# Revit family: 540_Sliding_Window_XO_Standard
name_source: partatom
category: Windows
revit_build: Autodesk Revit 2014 (Build: 20130308_1515(x64)
units: mm (PartAtom-declared; Revit-internal decimal feet)

## types (72) — shared parameters
Centered In Wall = Yes
Custom Sash Width Left = 600 mm  [stored 1.9685 ft]
Default Sill Height = 800 mm
Description = Sliding window, XO
Equal Sash Width = Yes
Frame Thickness = 54 mm  [stored 0.177165 ft]
Limit Sash Height Max = 1500 mm  [stored 4.92126 ft]
Limit Sash Height Min = 300 mm  [stored 0.984252 ft]
Limit Sash Width Max = 1200 mm
Limit Sash Width Min = 300 mm  [stored 0.984252 ft]
Limit Window Height Max = 1580 mm
Limit Window Height Min = 380 mm
Limit Window Width Max = 2418 mm
Limit Window Width Min = 618 mm
Manufacturer = Crealco
Model = 540
Rough Width = 3 mm  [stored 0.00984252 ft]
Sash Frame Seal = 3 mm  [stored 0.00984252 ft]
URL = http://www.crealco.co.za
Wall Closure = By host
zero-valued in all types: Custom Frame Offset From Exterior

## per-type parameters (varying)
- 540SW-0906XO-1000Pa: Area Left Sash Glazing=0.13 m²; Area Right Sash Glazing=0.13 m²; Clearvue SHGC Value=0.399; Clearvue U Value=7.41; Custom Windload=1000 mm  [stored 3.28084 ft]; Custom Window Height=590 mm  [stored 1.9357 ft]; Custom Window Width=890 mm  [stored 2.91995 ft]; Energy Advantage SHGC Value=0.361; Energy Advantage U Value=6.43; Heavy Duty Interlocker=No; Height=590 mm  [stored 1.9357 ft]; Intruderprufe LowE SHGC Value=0.339; Intruderprufe LowE U Value=6.32; Intruderprufe SHGC Value=0.378; Intruderprufe U Value=7.24; Is Heavy Duty Interlocker=0 mm  [stored 0 ft]; Limit Sash Width Left Max=572 mm; Limit Sash Width Left Min=300 mm  [stored 0.984252 ft]; Max Pane Area=0.13 m²; Sash Height=510 mm; Sash Width Left=436 mm; Sash Width Right=436 mm; Standard Interlocker=Yes; Width=890 mm  [stored 2.91995 ft]; Windload Design=1000 mm  [stored 3.28084 ft]
- 540SW-1206XO-1000Pa: Area Left Sash Glazing=0.19 m²; Area Right Sash Glazing=0.19 m²; Clearvue SHGC Value=0.44; Clearvue U Value=7.19; Custom Windload=1000 mm  [stored 3.28084 ft]; Custom Window Height=590 mm  [stored 1.9357 ft]; Custom Window Width=1190 mm  [stored 3.9042 ft]; Energy Advantage SHGC Value=0.397; Energy Advantage U Value=6.12; Heavy Duty Interlocker=No; Height=590 mm  [stored 1.9357 ft]; Intruderprufe LowE SHGC Value=0.372; Intruderprufe LowE U Value=6.02; Intruderprufe SHGC Value=0.416; Intruderprufe U Value=7.04; Is Heavy Duty Interlocker=0 mm  [stored 0 ft]; Limit Sash Width Left Max=872 mm; Limit Sash Width Left Min=300 mm  [stored 0.984252 ft]; Max Pane Area=0.19 m²; Sash Height=510 mm; Sash Width Left=586 mm; Sash Width Right=586 mm; Standard Interlocker=Yes; Width=1190 mm  [stored 3.9042 ft]; Windload Design=1000 mm  [stored 3.28084 ft]
- 540SW-1506XO-1000Pa: Area Left Sash Glazing=0.25 m²; Area Right Sash Glazing=0.25 m²; Clearvue SHGC Value=0.464; Clearvue U Value=7.07; Custom Windload=1000 mm  [stored 3.28084 ft]; Custom Window Height=590 mm  [stored 1.9357 ft]; Custom Window Width=1490 mm  [stored 4.88845 ft]; Energy Advantage SHGC Value=0.418; Energy Advantage U Value=5.93; Heavy Duty Interlocker=No; Height=590 mm  [stored 1.9357 ft]; Intruderprufe LowE SHGC Value=0.392; Intruderprufe LowE U Value=5.83; Intruderprufe SHGC Value=0.439; Intruderprufe U Value=6.93; Is Heavy Duty Interlocker=0 mm  [stored 0 ft]; Limit Sash Width Left Max=1172 mm; Limit Sash Width Left Min=300 mm  [stored 0.984252 ft]; Max Pane Area=0.25 m²; Sash Height=510 mm; Sash Width Left=736 mm; Sash Width Right=736 mm; Standard Interlocker=Yes; Width=1490 mm  [stored 4.88845 ft]; Windload Design=1000 mm  [stored 3.28084 ft]
- 540SW-1806XO-1000Pa: Area Left Sash Glazing=0.31 m²; Area Right Sash Glazing=0.31 m²; Clearvue SHGC Value=0.481; Clearvue U Value=6.98; Custom Windload=1000 mm  [stored 3.28084 ft]; Custom Window Height=590 mm  [stored 1.9357 ft]; Custom Window Width=1790 mm  [stored 5.8727 ft]; Energy Advantage SHGC Value=0.433; Energy Advantage U Value=5.81; Heavy Duty Interlocker=No; Height=590 mm  [stored 1.9357 ft]; Intruderprufe LowE SHGC Value=0.405; Intruderprufe LowE U Value=5.71; Intruderprufe SHGC Value=0.454; Intruderprufe U Value=6.85; Is Heavy Duty Interlocker=0 mm  [stored 0 ft]; Limit Sash Width Left Max=1200 mm; Limit Sash Width Left Min=572 mm; Max Pane Area=0.31 m²; Sash Height=510 mm; Sash Width Left=886 mm; Sash Width Right=886 mm; Standard Interlocker=Yes; Width=1790 mm  [stored 5.8727 ft]; Windload Design=1000 mm  [stored 3.28084 ft]
- 540SW-2106XO-1000Pa: Area Left Sash Glazing=0.37 m²; Area Right Sash Glazing=0.37 m²; Clearvue SHGC Value=0.492; Clearvue U Value=6.92; Custom Windload=1000 mm  [stored 3.28084 ft]; Custom Window Height=590 mm  [stored 1.9357 ft]; Custom Window Width=2090 mm  [stored 6.85696 ft]; Energy Advantage SHGC Value=0.443; Energy Advantage U Value=5.72; Heavy Duty Interlocker=No; Height=590 mm  [stored 1.9357 ft]; Intruderprufe LowE SHGC Value=0.414; Intruderprufe LowE U Value=5.62; Intruderprufe SHGC Value=0.465; Intruderprufe U Value=6.79; Is Heavy Duty Interlocker=0 mm  [stored 0 ft]; Limit Sash Width Left Max=1200 mm; Limit Sash Width Left Min=872 mm; Max Pane Area=0.37 m²; Sash Height=510 mm; Sash Width Left=1036 mm; Sash Width Right=1036 mm; Standard Interlocker=Yes; Width=2090 mm  [stored 6.85696 ft]; Windload Design=1000 mm  [stored 3.28084 ft]
- 540SW-2406XO-1000Pa: Area Left Sash Glazing=0.43 m²; Area Right Sash Glazing=0.43 m²; Clearvue SHGC Value=0.501; Clearvue U Value=6.88; Custom Windload=1000 mm  [stored 3.28084 ft]; Custom Window Height=590 mm  [stored 1.9357 ft]; Custom Window Width=2390 mm  [stored 7.84121 ft]; Energy Advantage SHGC Value=0.45; Energy Advantage U Value=5.65; Heavy Duty Interlocker=No; Height=590 mm  [stored 1.9357 ft]; Intruderprufe LowE SHGC Value=0.421; Intruderprufe LowE U Value=5.56; Intruderprufe SHGC Value=0.473; Intruderprufe U Value=6.75; Is Heavy Duty Interlocker=0 mm  [stored 0 ft]; Limit Sash Width Left Max=1200 mm; Limit Sash Width Left Min=1172 mm; Max Pane Area=0.43 m²; Sash Height=510 mm; Sash Width Left=1186 mm; Sash Width Right=1186 mm; Standard Interlocker=Yes; Width=2390 mm  [stored 7.84121 ft]; Windload Design=1000 mm  [stored 3.28084 ft]
- 540SW-0909XO-1000Pa: Area Left Sash Glazing=0.23 m²; Area Right Sash Glazing=0.23 m²; Clearvue SHGC Value=0.465; Clearvue U Value=7.33; Custom Windload=1000 mm  [stored 3.28084 ft]; Custom Window Height=890 mm  [stored 2.91995 ft]; Custom Window Width=890 mm  [stored 2.91995 ft]; Energy Advantage SHGC Value=0.419; Energy Advantage U Value=6.16; Heavy Duty Interlocker=No; Height=890 mm  [stored 2.91995 ft]; Intruderprufe LowE SHGC Value=0.392; Intruderprufe LowE U Value=6.06; Intruderprufe SHGC Value=0.44; Intruderprufe U Value=7.16; Is Heavy Duty Interlocker=0 mm  [stored 0 ft]; Limit Sash Width Left Max=572 mm; Limit Sash Width Left Min=300 mm  [stored 0.984252 ft]; Max Pane Area=0.23 m²; Sash Height=810 mm  [stored 2.65748 ft]; Sash Width Left=436 mm; Sash Width Right=436 mm; Standard Interlocker=Yes; Width=890 mm  [stored 2.91995 ft]; Windload Design=1000 mm  [stored 3.28084 ft]
- 540SW-1209XO-1000Pa: Area Left Sash Glazing=0.34 m²; Area Right Sash Glazing=0.34 m²; Clearvue SHGC Value=0.514; Clearvue U Value=7.08; Custom Windload=1000 mm  [stored 3.28084 ft]; Custom Window Height=890 mm  [stored 2.91995 ft]; Custom Window Width=1190 mm  [stored 3.9042 ft]; Energy Advantage SHGC Value=0.462; Energy Advantage U Value=5.79; Heavy Duty Interlocker=No; Height=890 mm  [stored 2.91995 ft]; Intruderprufe LowE SHGC Value=0.432; Intruderprufe LowE U Value=5.69; Intruderprufe SHGC Value=0.485; Intruderprufe U Value=6.92; Is Heavy Duty Interlocker=0 mm  [stored 0 ft]; Limit Sash Width Left Max=872 mm; Limit Sash Width Left Min=300 mm  [stored 0.984252 ft]; Max Pane Area=0.34 m²; Sash Height=810 mm  [stored 2.65748 ft]; Sash Width Left=586 mm; Sash Width Right=586 mm; Standard Interlocker=Yes; Width=1190 mm  [stored 3.9042 ft]; Windload Design=1000 mm  [stored 3.28084 ft]
- 540SW-1509XO-1000Pa: Area Left Sash Glazing=0.44 m²; Area Right Sash Glazing=0.44 m²; Clearvue SHGC Value=0.543; Clearvue U Value=6.93; Custom Windload=1000 mm  [stored 3.28084 ft]; Custom Window Height=890 mm  [stored 2.91995 ft]; Custom Window Width=1490 mm  [stored 4.88845 ft]; Energy Advantage SHGC Value=0.488; Energy Advantage U Value=5.57; Heavy Duty Interlocker=No; Height=890 mm  [stored 2.91995 ft]; Intruderprufe LowE SHGC Value=0.456; Intruderprufe LowE U Value=5.47; Intruderprufe SHGC Value=0.512; Intruderprufe U Value=6.78; Is Heavy Duty Interlocker=0 mm  [stored 0 ft]; Limit Sash Width Left Max=1172 mm; Limit Sash Width Left Min=300 mm  [stored 0.984252 ft]; Max Pane Area=0.44 m²; Sash Height=810 mm  [stored 2.65748 ft]; Sash Width Left=736 mm; Sash Width Right=736 mm; Standard Interlocker=Yes; Width=1490 mm  [stored 4.88845 ft]; Windload Design=1000 mm  [stored 3.28084 ft]
- 540SW-1809XO-1000Pa: Area Left Sash Glazing=0.55 m²; Area Right Sash Glazing=0.55 m²; Clearvue SHGC Value=0.562; Clearvue U Value=6.83; Custom Windload=1000 mm  [stored 3.28084 ft]; Custom Window Height=890 mm  [stored 2.91995 ft]; Custom Window Width=1790 mm  [stored 5.8727 ft]; Energy Advantage SHGC Value=0.505; Energy Advantage U Value=5.42; Heavy Duty Interlocker=No; Height=890 mm  [stored 2.91995 ft]; Intruderprufe LowE SHGC Value=0.471; Intruderprufe LowE U Value=5.33; Intruderprufe SHGC Value=0.531; Intruderprufe U Value=6.68; Is Heavy Duty Interlocker=0 mm  [stored 0 ft]; Limit Sash Width Left Max=1200 mm; Limit Sash Width Left Min=572 mm; Max Pane Area=0.55 m²; Sash Height=810 mm  [stored 2.65748 ft]; Sash Width Left=886 mm; Sash Width Right=886 mm; Standard Interlocker=Yes; Width=1790 mm  [stored 5.8727 ft]; Windload Design=1000 mm  [stored 3.28084 ft]
- 540SW-2109XO-1000Pa: Area Left Sash Glazing=0.65 m²; Area Right Sash Glazing=0.65 m²; Clearvue SHGC Value=0.576; Clearvue U Value=6.76; Custom Windload=1000 mm  [stored 3.28084 ft]; Custom Window Height=890 mm  [stored 2.91995 ft]; Custom Window Width=2090 mm  [stored 6.85696 ft]; Energy Advantage SHGC Value=0.517; Energy Advantage U Value=5.32; Heavy Duty Interlocker=No; Height=890 mm  [stored 2.91995 ft]; Intruderprufe LowE SHGC Value=0.483; Intruderprufe LowE U Value=5.22; Intruderprufe SHGC Value=0.543; Intruderprufe U Value=6.62; Is Heavy Duty Interlocker=0 mm  [stored 0 ft]; Limit Sash Width Left Max=1200 mm; Limit Sash Width Left Min=872 mm; Max Pane Area=0.65 m²; Sash Height=810 mm  [stored 2.65748 ft]; Sash Width Left=1036 mm; Sash Width Right=1036 mm; Standard Interlocker=Yes; Width=2090 mm  [stored 6.85696 ft]; Windload Design=1000 mm  [stored 3.28084 ft]
- 540SW-2409XO-1000Pa: Area Left Sash Glazing=0.76 m²; Area Right Sash Glazing=0.76 m²; Clearvue SHGC Value=0.586; Clearvue U Value=6.7; Custom Windload=1000 mm  [stored 3.28084 ft]; Custom Window Height=890 mm  [stored 2.91995 ft]; Custom Window Width=2390 mm  [stored 7.84121 ft]; Energy Advantage SHGC Value=0.526; Energy Advantage U Value=5.24; Heavy Duty Interlocker=No; Height=890 mm  [stored 2.91995 ft]; Intruderprufe LowE SHGC Value=0.491; Intruderprufe LowE U Value=5.15; Intruderprufe SHGC Value=0.553; Intruderprufe U Value=6.57; Is Heavy Duty Interlocker=0 mm  [stored 0 ft]; Limit Sash Width Left Max=1200 mm; Limit Sash Width Left Min=1172 mm; Max Pane Area=0.76 m²; Sash Height=810 mm  [stored 2.65748 ft]; Sash Width Left=1186 mm; Sash Width Right=1186 mm; Standard Interlocker=Yes; Width=2390 mm  [stored 7.84121 ft]; Windload Design=1000 mm  [stored 3.28084 ft]
- 540SW-0912XO-1000Pa: Area Left Sash Glazing=0.33 m²; Area Right Sash Glazing=0.33 m²; Clearvue SHGC Value=0.497; Clearvue U Value=7.29; Custom Windload=1000 mm  [stored 3.28084 ft]; Custom Window Height=1190 mm  [stored 3.9042 ft]; Custom Window Width=890 mm  [stored 2.91995 ft]; Energy Advantage SHGC Value=0.447; Energy Advantage U Value=6.02; Heavy Duty Interlocker=No; Height=1190 mm  [stored 3.9042 ft]; Intruderprufe LowE SHGC Value=0.419; Intruderprufe LowE U Value=5.92; Intruderprufe SHGC Value=0.47; Intruderprufe U Value=7.12; Is Heavy Duty Interlocker=0 mm  [stored 0 ft]; Limit Sash Width Left Max=572 mm; Limit Sash Width Left Min=300 mm  [stored 0.984252 ft]; Max Pane Area=0.33 m²; Sash Height=1110 mm  [stored 3.64173 ft]; Sash Width Left=436 mm; Sash Width Right=436 mm; Standard Interlocker=Yes; Width=890 mm  [stored 2.91995 ft]; Windload Design=1000 mm  [stored 3.28084 ft]
- 540SW-1212XO-1000Pa: Area Left Sash Glazing=0.48 m²; Area Right Sash Glazing=0.48 m²; Clearvue SHGC Value=0.55; Clearvue U Value=7.02; Custom Windload=1000 mm  [stored 3.28084 ft]; Custom Window Height=1190 mm  [stored 3.9042 ft]; Custom Window Width=1190 mm  [stored 3.9042 ft]; Energy Advantage SHGC Value=0.494; Energy Advantage U Value=5.62; Heavy Duty Interlocker=No; Height=1190 mm  [stored 3.9042 ft]; Intruderprufe LowE SHGC Value=0.462; Intruderprufe LowE U Value=5.53; Intruderprufe SHGC Value=0.519; Intruderprufe U Value=6.86; Is Heavy Duty Interlocker=0 mm  [stored 0 ft]; Limit Sash Width Left Max=872 mm; Limit Sash Width Left Min=300 mm  [stored 0.984252 ft]; Max Pane Area=0.48 m²; Sash Height=1110 mm  [stored 3.64173 ft]; Sash Width Left=586 mm; Sash Width Right=586 mm; Standard Interlocker=Yes; Width=1190 mm  [stored 3.9042 ft]; Windload Design=1000 mm  [stored 3.28084 ft]
- 540SW-1512XO-1000Pa: Area Left Sash Glazing=0.63 m²; Area Right Sash Glazing=0.63 m²; Clearvue SHGC Value=0.582; Clearvue U Value=6.86; Custom Windload=1000 mm  [stored 3.28084 ft]; Custom Window Height=1190 mm  [stored 3.9042 ft]; Custom Window Width=1490 mm  [stored 4.88845 ft]; Energy Advantage SHGC Value=0.522; Energy Advantage U Value=5.39; Heavy Duty Interlocker=No; Height=1190 mm  [stored 3.9042 ft]; Intruderprufe LowE SHGC Value=0.487; Intruderprufe LowE U Value=5.29; Intruderprufe SHGC Value=0.549; Intruderprufe U Value=6.71; Is Heavy Duty Interlocker=0 mm  [stored 0 ft]; Limit Sash Width Left Max=1172 mm; Limit Sash Width Left Min=300 mm  [stored 0.984252 ft]; Max Pane Area=0.63 m²; Sash Height=1110 mm  [stored 3.64173 ft]; Sash Width Left=736 mm; Sash Width Right=736 mm; Standard Interlocker=Yes; Width=1490 mm  [stored 4.88845 ft]; Windload Design=1000 mm  [stored 3.28084 ft]
- 540SW-1812XO-1000Pa: Area Left Sash Glazing=0.78 m²; Area Right Sash Glazing=0.78 m²; Clearvue SHGC Value=0.603; Clearvue U Value=6.75; Custom Windload=1000 mm  [stored 3.28084 ft]; Custom Window Height=1190 mm  [stored 3.9042 ft]; Custom Window Width=1790 mm  [stored 5.8727 ft]; Energy Advantage SHGC Value=0.54; Energy Advantage U Value=5.23; Heavy Duty Interlocker=No; Height=1190 mm  [stored 3.9042 ft]; Intruderprufe LowE SHGC Value=0.504; Intruderprufe LowE U Value=5.14; Intruderprufe SHGC Value=0.568; Intruderprufe U Value=6.61; Is Heavy Duty Interlocker=0 mm  [stored 0 ft]; Limit Sash Width Left Max=1200 mm; Limit Sash Width Left Min=572 mm; Max Pane Area=0.78 m²; Sash Height=1110 mm  [stored 3.64173 ft]; Sash Width Left=886 mm; Sash Width Right=886 mm; Standard Interlocker=Yes; Width=1790 mm  [stored 5.8727 ft]; Windload Design=1000 mm  [stored 3.28084 ft]
- 540SW-2112XO-1000Pa: Area Left Sash Glazing=0.93 m²; Area Right Sash Glazing=0.93 m²; Clearvue SHGC Value=0.617; Clearvue U Value=6.68; Custom Windload=1000 mm  [stored 3.28084 ft]; Custom Window Height=1190 mm  [stored 3.9042 ft]; Custom Window Width=2090 mm  [stored 6.85696 ft]; Energy Advantage SHGC Value=0.554; Energy Advantage U Value=5.12; Heavy Duty Interlocker=No; Height=1190 mm  [stored 3.9042 ft]; Intruderprufe LowE SHGC Value=0.516; Intruderprufe LowE U Value=5.03; Intruderprufe SHGC Value=0.582; Intruderprufe U Value=6.53; Is Heavy Duty Interlocker=0 mm  [stored 0 ft]; Limit Sash Width Left Max=1200 mm; Limit Sash Width Left Min=872 mm; Max Pane Area=0.93 m²; Sash Height=1110 mm  [stored 3.64173 ft]; Sash Width Left=1036 mm; Sash Width Right=1036 mm; Standard Interlocker=Yes; Width=2090 mm  [stored 6.85696 ft]; Windload Design=1000 mm  [stored 3.28084 ft]
- 540SW-2412XO-1000Pa: Area Left Sash Glazing=1.08 m²; Area Right Sash Glazing=1.08 m²; Clearvue SHGC Value=0.629; Clearvue U Value=6.62; Custom Windload=1000 mm  [stored 3.28084 ft]; Custom Window Height=1190 mm  [stored 3.9042 ft]; Custom Window Width=2390 mm  [stored 7.84121 ft]; Energy Advantage SHGC Value=0.564; Energy Advantage U Value=5.03; Heavy Duty Interlocker=No; Height=1190 mm  [stored 3.9042 ft]; Intruderprufe LowE SHGC Value=0.525; Intruderprufe LowE U Value=4.94; Intruderprufe SHGC Value=0.593; Intruderprufe U Value=6.48; Is Heavy Duty Interlocker=0 mm  [stored 0 ft]; Limit Sash Width Left Max=1200 mm; Limit Sash Width Left Min=1172 mm; Max Pane Area=1.08 m²; Sash Height=1110 mm  [stored 3.64173 ft]; Sash Width Left=1186 mm; Sash Width Right=1186 mm; Standard Interlocker=Yes; Width=2390 mm  [stored 7.84121 ft]; Windload Design=1000 mm  [stored 3.28084 ft]
- 540SW-0915XO-1000Pa: Area Left Sash Glazing=0.43 m²; Area Right Sash Glazing=0.43 m²; Clearvue SHGC Value=0.517; Clearvue U Value=7.27; Custom Windload=1000 mm  [stored 3.28084 ft]; Custom Window Height=1490 mm  [stored 4.88845 ft]; Custom Window Width=890 mm  [stored 2.91995 ft]; Energy Advantage SHGC Value=0.465; Energy Advantage U Value=5.94; Heavy Duty Interlocker=No; Height=1490 mm  [stored 4.88845 ft]; Intruderprufe LowE SHGC Value=0.435; Intruderprufe LowE U Value=5.84; Intruderprufe SHGC Value=0.488; Intruderprufe U Value=7.09; Is Heavy Duty Interlocker=0 mm  [stored 0 ft]; Limit Sash Width Left Max=572 mm; Limit Sash Width Left Min=300 mm  [stored 0.984252 ft]; Max Pane Area=0.43 m²; Sash Height=1410 mm; Sash Width Left=436 mm; Sash Width Right=436 mm; Standard Interlocker=Yes; Width=890 mm  [stored 2.91995 ft]; Windload Design=1000 mm  [stored 3.28084 ft]
- 540SW-1215XO-1000Pa: Area Left Sash Glazing=0.62 m²; Area Right Sash Glazing=0.62 m²; Clearvue SHGC Value=0.572; Clearvue U Value=6.99; Custom Windload=1000 mm  [stored 3.28084 ft]; Custom Window Height=1490 mm  [stored 4.88845 ft]; Custom Window Width=1190 mm  [stored 3.9042 ft]; Energy Advantage SHGC Value=0.513; Energy Advantage U Value=5.53; Heavy Duty Interlocker=No; Height=1490 mm  [stored 4.88845 ft]; Intruderprufe LowE SHGC Value=0.479; Intruderprufe LowE U Value=5.43; Intruderprufe SHGC Value=0.54; Intruderprufe U Value=6.82; Is Heavy Duty Interlocker=0 mm  [stored 0 ft]; Limit Sash Width Left Max=872 mm; Limit Sash Width Left Min=300 mm  [stored 0.984252 ft]; Max Pane Area=0.62 m²; Sash Height=1410 mm; Sash Width Left=586 mm; Sash Width Right=586 mm; Standard Interlocker=Yes; Width=1190 mm  [stored 3.9042 ft]; Windload Design=1000 mm  [stored 3.28084 ft]
- 540SW-1515XO-1000Pa: Area Left Sash Glazing=0.82 m²; Area Right Sash Glazing=0.82 m²; Clearvue SHGC Value=0.605; Clearvue U Value=6.82; Custom Windload=1000 mm  [stored 3.28084 ft]; Custom Window Height=1490 mm  [stored 4.88845 ft]; Custom Window Width=1490 mm  [stored 4.88845 ft]; Energy Advantage SHGC Value=0.542; Energy Advantage U Value=5.28; Heavy Duty Interlocker=Yes; Height=1490 mm  [stored 4.88845 ft]; Intruderprufe LowE SHGC Value=0.506; Intruderprufe LowE U Value=5.19; Intruderprufe SHGC Value=0.571; Intruderprufe U Value=6.66; Is Heavy Duty Interlocker=1 mm  [stored 0.00328084 ft]; Limit Sash Width Left Max=1172 mm; Limit Sash Width Left Min=300 mm  [stored 0.984252 ft]; Max Pane Area=0.82 m²; Sash Height=1410 mm; Sash Width Left=736 mm; Sash Width Right=736 mm; Standard Interlocker=No; Width=1490 mm  [stored 4.88845 ft]; Windload Design=1000 mm  [stored 3.28084 ft]
- 540SW-1815XO-1000Pa: Area Left Sash Glazing=1.01 m²; Area Right Sash Glazing=1.01 m²; Clearvue SHGC Value=0.627; Clearvue U Value=6.71; Custom Windload=1000 mm  [stored 3.28084 ft]; Custom Window Height=1490 mm  [stored 4.88845 ft]; Custom Window Width=1790 mm  [stored 5.8727 ft]; Energy Advantage SHGC Value=0.562; Energy Advantage U Value=5.11; Heavy Duty Interlocker=Yes; Height=1490 mm  [stored 4.88845 ft]; Intruderprufe LowE SHGC Value=0.524; Intruderprufe LowE U Value=5.02; Intruderprufe SHGC Value=0.591; Intruderprufe U Value=6.56; Is Heavy Duty Interlocker=1 mm  [stored 0.00328084 ft]; Limit Sash Width Left Max=1200 mm; Limit Sash Width Left Min=572 mm; Max Pane Area=1.01 m²; Sash Height=1410 mm; Sash Width Left=886 mm; Sash Width Right=886 mm; Standard Interlocker=No; Width=1790 mm  [stored 5.8727 ft]; Windload Design=1000 mm  [stored 3.28084 ft]
- 540SW-2115XO-1000Pa: Area Left Sash Glazing=1.21 m²; Area Right Sash Glazing=1.21 m²; Clearvue SHGC Value=0.642; Clearvue U Value=6.63; Custom Windload=1000 mm  [stored 3.28084 ft]; Custom Window Height=1490 mm  [stored 4.88845 ft]; Custom Window Width=2090 mm  [stored 6.85696 ft]; Energy Advantage SHGC Value=0.576; Energy Advantage U Value=5; Heavy Duty Interlocker=Yes; Height=1490 mm  [stored 4.88845 ft]; Intruderprufe LowE SHGC Value=0.536; Intruderprufe LowE U Value=4.91; Intruderprufe SHGC Value=0.606; Intruderprufe U Value=6.48; Is Heavy Duty Interlocker=1 mm  [stored 0.00328084 ft]; Limit Sash Width Left Max=1200 mm; Limit Sash Width Left Min=872 mm; Max Pane Area=1.21 m²; Sash Height=1410 mm; Sash Width Left=1036 mm; Sash Width Right=1036 mm; Standard Interlocker=No; Width=2090 mm  [stored 6.85696 ft]; Windload Design=1000 mm  [stored 3.28084 ft]
- 540SW-2415XO-1000Pa: Area Left Sash Glazing=1.4 m²; Area Right Sash Glazing=1.4 m²; Clearvue SHGC Value=0.654; Clearvue U Value=6.57; Custom Windload=1000 mm  [stored 3.28084 ft]; Custom Window Height=1490 mm  [stored 4.88845 ft]; Custom Window Width=2390 mm  [stored 7.84121 ft]; Energy Advantage SHGC Value=0.586; Energy Advantage U Value=4.91; Heavy Duty Interlocker=Yes; Height=1490 mm  [stored 4.88845 ft]; Intruderprufe LowE SHGC Value=0.546; Intruderprufe LowE U Value=4.82; Intruderprufe SHGC Value=0.617; Intruderprufe U Value=6.43; Is Heavy Duty Interlocker=1 mm  [stored 0.00328084 ft]; Limit Sash Width Left Max=1200 mm; Limit Sash Width Left Min=1172 mm; Max Pane Area=1.4 m²; Sash Height=1410 mm; Sash Width Left=1186 mm; Sash Width Right=1186 mm; Standard Interlocker=No; Width=2390 mm  [stored 7.84121 ft]; Windload Design=1000 mm  [stored 3.28084 ft]
- 540SW-0906XO-1500Pa: Area Left Sash Glazing=0.13 m²; Area Right Sash Glazing=0.13 m²; Clearvue SHGC Value=0.399; Clearvue U Value=7.41; Custom Windload=1500 mm  [stored 4.92126 ft]; Custom Window Height=590 mm  [stored 1.9357 ft]; Custom Window Width=890 mm  [stored 2.91995 ft]; Energy Advantage SHGC Value=0.361; Energy Advantage U Value=6.43; Heavy Duty Interlocker=No; Height=590 mm  [stored 1.9357 ft]; Intruderprufe LowE SHGC Value=0.339; Intruderprufe LowE U Value=6.32; Intruderprufe SHGC Value=0.378; Intruderprufe U Value=7.24; Is Heavy Duty Interlocker=0 mm  [stored 0 ft]; Limit Sash Width Left Max=572 mm; Limit Sash Width Left Min=300 mm  [stored 0.984252 ft]; Max Pane Area=0.13 m²; Sash Height=510 mm; Sash Width Left=436 mm; Sash Width Right=436 mm; Standard Interlocker=Yes; Width=890 mm  [stored 2.91995 ft]; Windload Design=1500 mm  [stored 4.92126 ft]
- 540SW-0906XO-2000Pa: Area Left Sash Glazing=0.13 m²; Area Right Sash Glazing=0.13 m²; Clearvue SHGC Value=0.399; Clearvue U Value=7.41; Custom Windload=2000 mm  [stored 6.56168 ft]; Custom Window Height=590 mm  [stored 1.9357 ft]; Custom Window Width=890 mm  [stored 2.91995 ft]; Energy Advantage SHGC Value=0.361; Energy Advantage U Value=6.43; Heavy Duty Interlocker=No; Height=590 mm  [stored 1.9357 ft]; Intruderprufe LowE SHGC Value=0.339; Intruderprufe LowE U Value=6.32; Intruderprufe SHGC Value=0.378; Intruderprufe U Value=7.24; Is Heavy Duty Interlocker=0 mm  [stored 0 ft]; Limit Sash Width Left Max=572 mm; Limit Sash Width Left Min=300 mm  [stored 0.984252 ft]; Max Pane Area=0.13 m²; Sash Height=510 mm; Sash Width Left=436 mm; Sash Width Right=436 mm; Standard Interlocker=Yes; Width=890 mm  [stored 2.91995 ft]; Windload Design=2000 mm  [stored 6.56168 ft]
- 540SW-0909XO-1500Pa: Area Left Sash Glazing=0.23 m²; Area Right Sash Glazing=0.23 m²; Clearvue SHGC Value=0.465; Clearvue U Value=7.33; Custom Windload=1500 mm  [stored 4.92126 ft]; Custom Window Height=890 mm  [stored 2.91995 ft]; Custom Window Width=890 mm  [stored 2.91995 ft]; Energy Advantage SHGC Value=0.419; Energy Advantage U Value=6.16; Heavy Duty Interlocker=No; Height=890 mm  [stored 2.91995 ft]; Intruderprufe LowE SHGC Value=0.392; Intruderprufe LowE U Value=6.06; Intruderprufe SHGC Value=0.44; Intruderprufe U Value=7.16; Is Heavy Duty Interlocker=0 mm  [stored 0 ft]; Limit Sash Width Left Max=572 mm; Limit Sash Width Left Min=300 mm  [stored 0.984252 ft]; Max Pane Area=0.23 m²; Sash Height=810 mm  [stored 2.65748 ft]; Sash Width Left=436 mm; Sash Width Right=436 mm; Standard Interlocker=Yes; Width=890 mm  [stored 2.91995 ft]; Windload Design=1500 mm  [stored 4.92126 ft]
- 540SW-0909XO-2000Pa: Area Left Sash Glazing=0.23 m²; Area Right Sash Glazing=0.23 m²; Clearvue SHGC Value=0.465; Clearvue U Value=7.33; Custom Windload=2000 mm  [stored 6.56168 ft]; Custom Window Height=890 mm  [stored 2.91995 ft]; Custom Window Width=890 mm  [stored 2.91995 ft]; Energy Advantage SHGC Value=0.419; Energy Advantage U Value=6.16; Heavy Duty Interlocker=No; Height=890 mm  [stored 2.91995 ft]; Intruderprufe LowE SHGC Value=0.392; Intruderprufe LowE U Value=6.06; Intruderprufe SHGC Value=0.44; Intruderprufe U Value=7.16; Is Heavy Duty Interlocker=0 mm  [stored 0 ft]; Limit Sash Width Left Max=572 mm; Limit Sash Width Left Min=300 mm  [stored 0.984252 ft]; Max Pane Area=0.23 m²; Sash Height=810 mm  [stored 2.65748 ft]; Sash Width Left=436 mm; Sash Width Right=436 mm; Standard Interlocker=Yes; Width=890 mm  [stored 2.91995 ft]; Windload Design=2000 mm  [stored 6.56168 ft]
- 540SW-0912XO-1500Pa: Area Left Sash Glazing=0.33 m²; Area Right Sash Glazing=0.33 m²; Clearvue SHGC Value=0.497; Clearvue U Value=7.29; Custom Windload=1500 mm  [stored 4.92126 ft]; Custom Window Height=1190 mm  [stored 3.9042 ft]; Custom Window Width=890 mm  [stored 2.91995 ft]; Energy Advantage SHGC Value=0.447; Energy Advantage U Value=6.02; Heavy Duty Interlocker=No; Height=1190 mm  [stored 3.9042 ft]; Intruderprufe LowE SHGC Value=0.419; Intruderprufe LowE U Value=5.92; Intruderprufe SHGC Value=0.47; Intruderprufe U Value=7.12; Is Heavy Duty Interlocker=0 mm  [stored 0 ft]; Limit Sash Width Left Max=572 mm; Limit Sash Width Left Min=300 mm  [stored 0.984252 ft]; Max Pane Area=0.33 m²; Sash Height=1110 mm  [stored 3.64173 ft]; Sash Width Left=436 mm; Sash Width Right=436 mm; Standard Interlocker=Yes; Width=890 mm  [stored 2.91995 ft]; Windload Design=1500 mm  [stored 4.92126 ft]
- 540SW-0912XO-2000Pa: Area Left Sash Glazing=0.33 m²; Area Right Sash Glazing=0.33 m²; Clearvue SHGC Value=0.497; Clearvue U Value=7.29; Custom Windload=2000 mm  [stored 6.56168 ft]; Custom Window Height=1190 mm  [stored 3.9042 ft]; Custom Window Width=890 mm  [stored 2.91995 ft]; Energy Advantage SHGC Value=0.447; Energy Advantage U Value=6.02; Heavy Duty Interlocker=No; Height=1190 mm  [stored 3.9042 ft]; Intruderprufe LowE SHGC Value=0.419; Intruderprufe LowE U Value=5.92; Intruderprufe SHGC Value=0.47; Intruderprufe U Value=7.12; Is Heavy Duty Interlocker=0 mm  [stored 0 ft]; Limit Sash Width Left Max=572 mm; Limit Sash Width Left Min=300 mm  [stored 0.984252 ft]; Max Pane Area=0.33 m²; Sash Height=1110 mm  [stored 3.64173 ft]; Sash Width Left=436 mm; Sash Width Right=436 mm; Standard Interlocker=Yes; Width=890 mm  [stored 2.91995 ft]; Windload Design=2000 mm  [stored 6.56168 ft]
- 540SW-0915XO-1500Pa: Area Left Sash Glazing=0.43 m²; Area Right Sash Glazing=0.43 m²; Clearvue SHGC Value=0.517; Clearvue U Value=7.27; Custom Windload=1500 mm  [stored 4.92126 ft]; Custom Window Height=1490 mm  [stored 4.88845 ft]; Custom Window Width=890 mm  [stored 2.91995 ft]; Energy Advantage SHGC Value=0.465; Energy Advantage U Value=5.94; Heavy Duty Interlocker=Yes; Height=1490 mm  [stored 4.88845 ft]; Intruderprufe LowE SHGC Value=0.435; Intruderprufe LowE U Value=5.84; Intruderprufe SHGC Value=0.488; Intruderprufe U Value=7.09; Is Heavy Duty Interlocker=1 mm  [stored 0.00328084 ft]; Limit Sash Width Left Max=572 mm; Limit Sash Width Left Min=300 mm  [stored 0.984252 ft]; Max Pane Area=0.43 m²; Sash Height=1410 mm; Sash Width Left=436 mm; Sash Width Right=436 mm; Standard Interlocker=No; Width=890 mm  [stored 2.91995 ft]; Windload Design=1500 mm  [stored 4.92126 ft]
- 540SW-0915XO-2000Pa: Area Left Sash Glazing=0.43 m²; Area Right Sash Glazing=0.43 m²; Clearvue SHGC Value=0.517; Clearvue U Value=7.27; Custom Windload=2000 mm  [stored 6.56168 ft]; Custom Window Height=1490 mm  [stored 4.88845 ft]; Custom Window Width=890 mm  [stored 2.91995 ft]; Energy Advantage SHGC Value=0.465; Energy Advantage U Value=5.94; Heavy Duty Interlocker=Yes; Height=1490 mm  [stored 4.88845 ft]; Intruderprufe LowE SHGC Value=0.435; Intruderprufe LowE U Value=5.84; Intruderprufe SHGC Value=0.488; Intruderprufe U Value=7.09; Is Heavy Duty Interlocker=1 mm  [stored 0.00328084 ft]; Limit Sash Width Left Max=572 mm; Limit Sash Width Left Min=300 mm  [stored 0.984252 ft]; Max Pane Area=0.43 m²; Sash Height=1410 mm; Sash Width Left=436 mm; Sash Width Right=436 mm; Standard Interlocker=No; Width=890 mm  [stored 2.91995 ft]; Windload Design=2000 mm  [stored 6.56168 ft]
- 540SW-1206XO-1500Pa: Area Left Sash Glazing=0.19 m²; Area Right Sash Glazing=0.19 m²; Clearvue SHGC Value=0.44; Clearvue U Value=7.19; Custom Windload=1500 mm  [stored 4.92126 ft]; Custom Window Height=590 mm  [stored 1.9357 ft]; Custom Window Width=1190 mm  [stored 3.9042 ft]; Energy Advantage SHGC Value=0.397; Energy Advantage U Value=6.12; Heavy Duty Interlocker=No; Height=590 mm  [stored 1.9357 ft]; Intruderprufe LowE SHGC Value=0.372; Intruderprufe LowE U Value=6.02; Intruderprufe SHGC Value=0.416; Intruderprufe U Value=7.04; Is Heavy Duty Interlocker=0 mm  [stored 0 ft]; Limit Sash Width Left Max=872 mm; Limit Sash Width Left Min=300 mm  [stored 0.984252 ft]; Max Pane Area=0.19 m²; Sash Height=510 mm; Sash Width Left=586 mm; Sash Width Right=586 mm; Standard Interlocker=Yes; Width=1190 mm  [stored 3.9042 ft]; Windload Design=1500 mm  [stored 4.92126 ft]
- 540SW-1206XO-2000Pa: Area Left Sash Glazing=0.19 m²; Area Right Sash Glazing=0.19 m²; Clearvue SHGC Value=0.44; Clearvue U Value=7.19; Custom Windload=2000 mm  [stored 6.56168 ft]; Custom Window Height=590 mm  [stored 1.9357 ft]; Custom Window Width=1190 mm  [stored 3.9042 ft]; Energy Advantage SHGC Value=0.397; Energy Advantage U Value=6.12; Heavy Duty Interlocker=No; Height=590 mm  [stored 1.9357 ft]; Intruderprufe LowE SHGC Value=0.372; Intruderprufe LowE U Value=6.02; Intruderprufe SHGC Value=0.416; Intruderprufe U Value=7.04; Is Heavy Duty Interlocker=0 mm  [stored 0 ft]; Limit Sash Width Left Max=872 mm; Limit Sash Width Left Min=300 mm  [stored 0.984252 ft]; Max Pane Area=0.19 m²; Sash Height=510 mm; Sash Width Left=586 mm; Sash Width Right=586 mm; Standard Interlocker=Yes; Width=1190 mm  [stored 3.9042 ft]; Windload Design=2000 mm  [stored 6.56168 ft]
- 540SW-1209XO-1500Pa: Area Left Sash Glazing=0.34 m²; Area Right Sash Glazing=0.34 m²; Clearvue SHGC Value=0.514; Clearvue U Value=7.08; Custom Windload=1500 mm  [stored 4.92126 ft]; Custom Window Height=890 mm  [stored 2.91995 ft]; Custom Window Width=1190 mm  [stored 3.9042 ft]; Energy Advantage SHGC Value=0.462; Energy Advantage U Value=5.79; Heavy Duty Interlocker=No; Height=890 mm  [stored 2.91995 ft]; Intruderprufe LowE SHGC Value=0.432; Intruderprufe LowE U Value=5.69; Intruderprufe SHGC Value=0.485; Intruderprufe U Value=6.92; Is Heavy Duty Interlocker=0 mm  [stored 0 ft]; Limit Sash Width Left Max=872 mm; Limit Sash Width Left Min=300 mm  [stored 0.984252 ft]; Max Pane Area=0.34 m²; Sash Height=810 mm  [stored 2.65748 ft]; Sash Width Left=586 mm; Sash Width Right=586 mm; Standard Interlocker=Yes; Width=1190 mm  [stored 3.9042 ft]; Windload Design=1500 mm  [stored 4.92126 ft]
- 540SW-1209XO-2000Pa: Area Left Sash Glazing=0.34 m²; Area Right Sash Glazing=0.34 m²; Clearvue SHGC Value=0.514; Clearvue U Value=7.08; Custom Windload=2000 mm  [stored 6.56168 ft]; Custom Window Height=890 mm  [stored 2.91995 ft]; Custom Window Width=1190 mm  [stored 3.9042 ft]; Energy Advantage SHGC Value=0.462; Energy Advantage U Value=5.79; Heavy Duty Interlocker=No; Height=890 mm  [stored 2.91995 ft]; Intruderprufe LowE SHGC Value=0.432; Intruderprufe LowE U Value=5.69; Intruderprufe SHGC Value=0.485; Intruderprufe U Value=6.92; Is Heavy Duty Interlocker=0 mm  [stored 0 ft]; Limit Sash Width Left Max=872 mm; Limit Sash Width Left Min=300 mm  [stored 0.984252 ft]; Max Pane Area=0.34 m²; Sash Height=810 mm  [stored 2.65748 ft]; Sash Width Left=586 mm; Sash Width Right=586 mm; Standard Interlocker=Yes; Width=1190 mm  [stored 3.9042 ft]; Windload Design=2000 mm  [stored 6.56168 ft]
- 540SW-1212XO-1500Pa: Area Left Sash Glazing=0.48 m²; Area Right Sash Glazing=0.48 m²; Clearvue SHGC Value=0.55; Clearvue U Value=7.02; Custom Windload=1500 mm  [stored 4.92126 ft]; Custom Window Height=1190 mm  [stored 3.9042 ft]; Custom Window Width=1190 mm  [stored 3.9042 ft]; Energy Advantage SHGC Value=0.494; Energy Advantage U Value=5.62; Heavy Duty Interlocker=No; Height=1190 mm  [stored 3.9042 ft]; Intruderprufe LowE SHGC Value=0.462; Intruderprufe LowE U Value=5.53; Intruderprufe SHGC Value=0.519; Intruderprufe U Value=6.86; Is Heavy Duty Interlocker=0 mm  [stored 0 ft]; Limit Sash Width Left Max=872 mm; Limit Sash Width Left Min=300 mm  [stored 0.984252 ft]; Max Pane Area=0.48 m²; Sash Height=1110 mm  [stored 3.64173 ft]; Sash Width Left=586 mm; Sash Width Right=586 mm; Standard Interlocker=Yes; Width=1190 mm  [stored 3.9042 ft]; Windload Design=1500 mm  [stored 4.92126 ft]
- 540SW-1212XO-2000Pa: Area Left Sash Glazing=0.48 m²; Area Right Sash Glazing=0.48 m²; Clearvue SHGC Value=0.55; Clearvue U Value=7.02; Custom Windload=2000 mm  [stored 6.56168 ft]; Custom Window Height=1190 mm  [stored 3.9042 ft]; Custom Window Width=1190 mm  [stored 3.9042 ft]; Energy Advantage SHGC Value=0.494; Energy Advantage U Value=5.62; Heavy Duty Interlocker=No; Height=1190 mm  [stored 3.9042 ft]; Intruderprufe LowE SHGC Value=0.462; Intruderprufe LowE U Value=5.53; Intruderprufe SHGC Value=0.519; Intruderprufe U Value=6.86; Is Heavy Duty Interlocker=0 mm  [stored 0 ft]; Limit Sash Width Left Max=872 mm; Limit Sash Width Left Min=300 mm  [stored 0.984252 ft]; Max Pane Area=0.48 m²; Sash Height=1110 mm  [stored 3.64173 ft]; Sash Width Left=586 mm; Sash Width Right=586 mm; Standard Interlocker=Yes; Width=1190 mm  [stored 3.9042 ft]; Windload Design=2000 mm  [stored 6.56168 ft]
- 540SW-1215XO-1500Pa: Area Left Sash Glazing=0.62 m²; Area Right Sash Glazing=0.62 m²; Clearvue SHGC Value=0.572; Clearvue U Value=6.99; Custom Windload=1500 mm  [stored 4.92126 ft]; Custom Window Height=1490 mm  [stored 4.88845 ft]; Custom Window Width=1190 mm  [stored 3.9042 ft]; Energy Advantage SHGC Value=0.513; Energy Advantage U Value=5.53; Heavy Duty Interlocker=Yes; Height=1490 mm  [stored 4.88845 ft]; Intruderprufe LowE SHGC Value=0.479; Intruderprufe LowE U Value=5.43; Intruderprufe SHGC Value=0.54; Intruderprufe U Value=6.82; Is Heavy Duty Interlocker=1 mm  [stored 0.00328084 ft]; Limit Sash Width Left Max=872 mm; Limit Sash Width Left Min=300 mm  [stored 0.984252 ft]; Max Pane Area=0.62 m²; Sash Height=1410 mm; Sash Width Left=586 mm; Sash Width Right=586 mm; Standard Interlocker=No; Width=1190 mm  [stored 3.9042 ft]; Windload Design=1500 mm  [stored 4.92126 ft]
- 540SW-1215XO-2000Pa: Area Left Sash Glazing=0.62 m²; Area Right Sash Glazing=0.62 m²; Clearvue SHGC Value=0.572; Clearvue U Value=6.99; Custom Windload=2000 mm  [stored 6.56168 ft]; Custom Window Height=1490 mm  [stored 4.88845 ft]; Custom Window Width=1190 mm  [stored 3.9042 ft]; Energy Advantage SHGC Value=0.513; Energy Advantage U Value=5.53; Heavy Duty Interlocker=Yes; Height=1490 mm  [stored 4.88845 ft]; Intruderprufe LowE SHGC Value=0.479; Intruderprufe LowE U Value=5.43; Intruderprufe SHGC Value=0.54; Intruderprufe U Value=6.82; Is Heavy Duty Interlocker=1 mm  [stored 0.00328084 ft]; Limit Sash Width Left Max=872 mm; Limit Sash Width Left Min=300 mm  [stored 0.984252 ft]; Max Pane Area=0.62 m²; Sash Height=1410 mm; Sash Width Left=586 mm; Sash Width Right=586 mm; Standard Interlocker=No; Width=1190 mm  [stored 3.9042 ft]; Windload Design=2000 mm  [stored 6.56168 ft]
- 540SW-1506XO-1500Pa: Area Left Sash Glazing=0.25 m²; Area Right Sash Glazing=0.25 m²; Clearvue SHGC Value=0.464; Clearvue U Value=7.07; Custom Windload=1500 mm  [stored 4.92126 ft]; Custom Window Height=590 mm  [stored 1.9357 ft]; Custom Window Width=1490 mm  [stored 4.88845 ft]; Energy Advantage SHGC Value=0.418; Energy Advantage U Value=5.93; Heavy Duty Interlocker=No; Height=590 mm  [stored 1.9357 ft]; Intruderprufe LowE SHGC Value=0.392; Intruderprufe LowE U Value=5.83; Intruderprufe SHGC Value=0.439; Intruderprufe U Value=6.93; Is Heavy Duty Interlocker=0 mm  [stored 0 ft]; Limit Sash Width Left Max=1172 mm; Limit Sash Width Left Min=300 mm  [stored 0.984252 ft]; Max Pane Area=0.25 m²; Sash Height=510 mm; Sash Width Left=736 mm; Sash Width Right=736 mm; Standard Interlocker=Yes; Width=1490 mm  [stored 4.88845 ft]; Windload Design=1500 mm  [stored 4.92126 ft]
- 540SW-1506XO-2000Pa: Area Left Sash Glazing=0.25 m²; Area Right Sash Glazing=0.25 m²; Clearvue SHGC Value=0.464; Clearvue U Value=7.07; Custom Windload=2000 mm  [stored 6.56168 ft]; Custom Window Height=590 mm  [stored 1.9357 ft]; Custom Window Width=1490 mm  [stored 4.88845 ft]; Energy Advantage SHGC Value=0.418; Energy Advantage U Value=5.93; Heavy Duty Interlocker=No; Height=590 mm  [stored 1.9357 ft]; Intruderprufe LowE SHGC Value=0.392; Intruderprufe LowE U Value=5.83; Intruderprufe SHGC Value=0.439; Intruderprufe U Value=6.93; Is Heavy Duty Interlocker=0 mm  [stored 0 ft]; Limit Sash Width Left Max=1172 mm; Limit Sash Width Left Min=300 mm  [stored 0.984252 ft]; Max Pane Area=0.25 m²; Sash Height=510 mm; Sash Width Left=736 mm; Sash Width Right=736 mm; Standard Interlocker=Yes; Width=1490 mm  [stored 4.88845 ft]; Windload Design=2000 mm  [stored 6.56168 ft]
- 540SW-1509XO-1500Pa: Area Left Sash Glazing=0.44 m²; Area Right Sash Glazing=0.44 m²; Clearvue SHGC Value=0.543; Clearvue U Value=6.93; Custom Windload=1500 mm  [stored 4.92126 ft]; Custom Window Height=890 mm  [stored 2.91995 ft]; Custom Window Width=1490 mm  [stored 4.88845 ft]; Energy Advantage SHGC Value=0.488; Energy Advantage U Value=5.57; Heavy Duty Interlocker=No; Height=890 mm  [stored 2.91995 ft]; Intruderprufe LowE SHGC Value=0.456; Intruderprufe LowE U Value=5.47; Intruderprufe SHGC Value=0.512; Intruderprufe U Value=6.78; Is Heavy Duty Interlocker=0 mm  [stored 0 ft]; Limit Sash Width Left Max=1172 mm; Limit Sash Width Left Min=300 mm  [stored 0.984252 ft]; Max Pane Area=0.44 m²; Sash Height=810 mm  [stored 2.65748 ft]; Sash Width Left=736 mm; Sash Width Right=736 mm; Standard Interlocker=Yes; Width=1490 mm  [stored 4.88845 ft]; Windload Design=1500 mm  [stored 4.92126 ft]
- 540SW-1509XO-2000Pa: Area Left Sash Glazing=0.44 m²; Area Right Sash Glazing=0.44 m²; Clearvue SHGC Value=0.543; Clearvue U Value=6.93; Custom Windload=2000 mm  [stored 6.56168 ft]; Custom Window Height=890 mm  [stored 2.91995 ft]; Custom Window Width=1490 mm  [stored 4.88845 ft]; Energy Advantage SHGC Value=0.488; Energy Advantage U Value=5.57; Heavy Duty Interlocker=No; Height=890 mm  [stored 2.91995 ft]; Intruderprufe LowE SHGC Value=0.456; Intruderprufe LowE U Value=5.47; Intruderprufe SHGC Value=0.512; Intruderprufe U Value=6.78; Is Heavy Duty Interlocker=0 mm  [stored 0 ft]; Limit Sash Width Left Max=1172 mm; Limit Sash Width Left Min=300 mm  [stored 0.984252 ft]; Max Pane Area=0.44 m²; Sash Height=810 mm  [stored 2.65748 ft]; Sash Width Left=736 mm; Sash Width Right=736 mm; Standard Interlocker=Yes; Width=1490 mm  [stored 4.88845 ft]; Windload Design=2000 mm  [stored 6.56168 ft]
- 540SW-1512XO-1500Pa: Area Left Sash Glazing=0.63 m²; Area Right Sash Glazing=0.63 m²; Clearvue SHGC Value=0.582; Clearvue U Value=6.86; Custom Windload=1500 mm  [stored 4.92126 ft]; Custom Window Height=1190 mm  [stored 3.9042 ft]; Custom Window Width=1490 mm  [stored 4.88845 ft]; Energy Advantage SHGC Value=0.522; Energy Advantage U Value=5.39; Heavy Duty Interlocker=No; Height=1190 mm  [stored 3.9042 ft]; Intruderprufe LowE SHGC Value=0.487; Intruderprufe LowE U Value=5.29; Intruderprufe SHGC Value=0.549; Intruderprufe U Value=6.71; Is Heavy Duty Interlocker=0 mm  [stored 0 ft]; Limit Sash Width Left Max=1172 mm; Limit Sash Width Left Min=300 mm  [stored 0.984252 ft]; Max Pane Area=0.63 m²; Sash Height=1110 mm  [stored 3.64173 ft]; Sash Width Left=736 mm; Sash Width Right=736 mm; Standard Interlocker=Yes; Width=1490 mm  [stored 4.88845 ft]; Windload Design=1500 mm  [stored 4.92126 ft]
- 540SW-1512XO-2000Pa: Area Left Sash Glazing=0.63 m²; Area Right Sash Glazing=0.63 m²; Clearvue SHGC Value=0.582; Clearvue U Value=6.86; Custom Windload=2000 mm  [stored 6.56168 ft]; Custom Window Height=1190 mm  [stored 3.9042 ft]; Custom Window Width=1490 mm  [stored 4.88845 ft]; Energy Advantage SHGC Value=0.522; Energy Advantage U Value=5.39; Heavy Duty Interlocker=Yes; Height=1190 mm  [stored 3.9042 ft]; Intruderprufe LowE SHGC Value=0.487; Intruderprufe LowE U Value=5.29; Intruderprufe SHGC Value=0.549; Intruderprufe U Value=6.71; Is Heavy Duty Interlocker=1 mm  [stored 0.00328084 ft]; Limit Sash Width Left Max=1172 mm; Limit Sash Width Left Min=300 mm  [stored 0.984252 ft]; Max Pane Area=0.63 m²; Sash Height=1110 mm  [stored 3.64173 ft]; Sash Width Left=736 mm; Sash Width Right=736 mm; Standard Interlocker=No; Width=1490 mm  [stored 4.88845 ft]; Windload Design=2000 mm  [stored 6.56168 ft]
- 540SW-1515XO-1500Pa: Area Left Sash Glazing=0.82 m²; Area Right Sash Glazing=0.82 m²; Clearvue SHGC Value=0.605; Clearvue U Value=6.82; Custom Windload=1500 mm  [stored 4.92126 ft]; Custom Window Height=1490 mm  [stored 4.88845 ft]; Custom Window Width=1490 mm  [stored 4.88845 ft]; Energy Advantage SHGC Value=0.542; Energy Advantage U Value=5.28; Heavy Duty Interlocker=Yes; Height=1490 mm  [stored 4.88845 ft]; Intruderprufe LowE SHGC Value=0.506; Intruderprufe LowE U Value=5.19; Intruderprufe SHGC Value=0.571; Intruderprufe U Value=6.66; Is Heavy Duty Interlocker=1 mm  [stored 0.00328084 ft]; Limit Sash Width Left Max=1172 mm; Limit Sash Width Left Min=300 mm  [stored 0.984252 ft]; Max Pane Area=0.82 m²; Sash Height=1410 mm; Sash Width Left=736 mm; Sash Width Right=736 mm; Standard Interlocker=No; Width=1490 mm  [stored 4.88845 ft]; Windload Design=1500 mm  [stored 4.92126 ft]
- 540SW-1515XO-2000Pa: Area Left Sash Glazing=0.82 m²; Area Right Sash Glazing=0.82 m²; Clearvue SHGC Value=0.605; Clearvue U Value=6.82; Custom Windload=2000 mm  [stored 6.56168 ft]; Custom Window Height=1490 mm  [stored 4.88845 ft]; Custom Window Width=1490 mm  [stored 4.88845 ft]; Energy Advantage SHGC Value=0.542; Energy Advantage U Value=5.28; Heavy Duty Interlocker=Yes; Height=1490 mm  [stored 4.88845 ft]; Intruderprufe LowE SHGC Value=0.506; Intruderprufe LowE U Value=5.19; Intruderprufe SHGC Value=0.571; Intruderprufe U Value=6.66; Is Heavy Duty Interlocker=1 mm  [stored 0.00328084 ft]; Limit Sash Width Left Max=1172 mm; Limit Sash Width Left Min=300 mm  [stored 0.984252 ft]; Max Pane Area=0.82 m²; Sash Height=1410 mm; Sash Width Left=736 mm; Sash Width Right=736 mm; Standard Interlocker=No; Width=1490 mm  [stored 4.88845 ft]; Windload Design=2000 mm  [stored 6.56168 ft]
- 540SW-1806XO-1500Pa: Area Left Sash Glazing=0.31 m²; Area Right Sash Glazing=0.31 m²; Clearvue SHGC Value=0.481; Clearvue U Value=6.98; Custom Windload=1500 mm  [stored 4.92126 ft]; Custom Window Height=590 mm  [stored 1.9357 ft]; Custom Window Width=1790 mm  [stored 5.8727 ft]; Energy Advantage SHGC Value=0.433; Energy Advantage U Value=5.81; Heavy Duty Interlocker=No; Height=590 mm  [stored 1.9357 ft]; Intruderprufe LowE SHGC Value=0.405; Intruderprufe LowE U Value=5.71; Intruderprufe SHGC Value=0.454; Intruderprufe U Value=6.85; Is Heavy Duty Interlocker=0 mm  [stored 0 ft]; Limit Sash Width Left Max=1200 mm; Limit Sash Width Left Min=572 mm; Max Pane Area=0.31 m²; Sash Height=510 mm; Sash Width Left=886 mm; Sash Width Right=886 mm; Standard Interlocker=Yes; Width=1790 mm  [stored 5.8727 ft]; Windload Design=1500 mm  [stored 4.92126 ft]
- 540SW-1806XO-2000Pa: Area Left Sash Glazing=0.31 m²; Area Right Sash Glazing=0.31 m²; Clearvue SHGC Value=0.481; Clearvue U Value=6.98; Custom Windload=2000 mm  [stored 6.56168 ft]; Custom Window Height=590 mm  [stored 1.9357 ft]; Custom Window Width=1790 mm  [stored 5.8727 ft]; Energy Advantage SHGC Value=0.433; Energy Advantage U Value=5.81; Heavy Duty Interlocker=No; Height=590 mm  [stored 1.9357 ft]; Intruderprufe LowE SHGC Value=0.405; Intruderprufe LowE U Value=5.71; Intruderprufe SHGC Value=0.454; Intruderprufe U Value=6.85; Is Heavy Duty Interlocker=0 mm  [stored 0 ft]; Limit Sash Width Left Max=1200 mm; Limit Sash Width Left Min=572 mm; Max Pane Area=0.31 m²; Sash Height=510 mm; Sash Width Left=886 mm; Sash Width Right=886 mm; Standard Interlocker=Yes; Width=1790 mm  [stored 5.8727 ft]; Windload Design=2000 mm  [stored 6.56168 ft]
- 540SW-1809XO-1500Pa: Area Left Sash Glazing=0.55 m²; Area Right Sash Glazing=0.55 m²; Clearvue SHGC Value=0.562; Clearvue U Value=6.83; Custom Windload=1500 mm  [stored 4.92126 ft]; Custom Window Height=890 mm  [stored 2.91995 ft]; Custom Window Width=1790 mm  [stored 5.8727 ft]; Energy Advantage SHGC Value=0.505; Energy Advantage U Value=5.42; Heavy Duty Interlocker=No; Height=890 mm  [stored 2.91995 ft]; Intruderprufe LowE SHGC Value=0.471; Intruderprufe LowE U Value=5.33; Intruderprufe SHGC Value=0.531; Intruderprufe U Value=6.68; Is Heavy Duty Interlocker=0 mm  [stored 0 ft]; Limit Sash Width Left Max=1200 mm; Limit Sash Width Left Min=572 mm; Max Pane Area=0.55 m²; Sash Height=810 mm  [stored 2.65748 ft]; Sash Width Left=886 mm; Sash Width Right=886 mm; Standard Interlocker=Yes; Width=1790 mm  [stored 5.8727 ft]; Windload Design=1500 mm  [stored 4.92126 ft]
- 540SW-1809XO-2000Pa: Area Left Sash Glazing=0.55 m²; Area Right Sash Glazing=0.55 m²; Clearvue SHGC Value=0.562; Clearvue U Value=6.83; Custom Windload=2000 mm  [stored 6.56168 ft]; Custom Window Height=890 mm  [stored 2.91995 ft]; Custom Window Width=1790 mm  [stored 5.8727 ft]; Energy Advantage SHGC Value=0.505; Energy Advantage U Value=5.42; Heavy Duty Interlocker=No; Height=890 mm  [stored 2.91995 ft]; Intruderprufe LowE SHGC Value=0.471; Intruderprufe LowE U Value=5.33; Intruderprufe SHGC Value=0.531; Intruderprufe U Value=6.68; Is Heavy Duty Interlocker=0 mm  [stored 0 ft]; Limit Sash Width Left Max=1200 mm; Limit Sash Width Left Min=572 mm; Max Pane Area=0.55 m²; Sash Height=810 mm  [stored 2.65748 ft]; Sash Width Left=886 mm; Sash Width Right=886 mm; Standard Interlocker=Yes; Width=1790 mm  [stored 5.8727 ft]; Windload Design=2000 mm  [stored 6.56168 ft]
- 540SW-1812XO-1500Pa: Area Left Sash Glazing=0.78 m²; Area Right Sash Glazing=0.78 m²; Clearvue SHGC Value=0.603; Clearvue U Value=6.75; Custom Windload=1500 mm  [stored 4.92126 ft]; Custom Window Height=1190 mm  [stored 3.9042 ft]; Custom Window Width=1790 mm  [stored 5.8727 ft]; Energy Advantage SHGC Value=0.54; Energy Advantage U Value=5.23; Heavy Duty Interlocker=No; Height=1190 mm  [stored 3.9042 ft]; Intruderprufe LowE SHGC Value=0.504; Intruderprufe LowE U Value=5.14; Intruderprufe SHGC Value=0.568; Intruderprufe U Value=6.61; Is Heavy Duty Interlocker=0 mm  [stored 0 ft]; Limit Sash Width Left Max=1200 mm; Limit Sash Width Left Min=572 mm; Max Pane Area=0.78 m²; Sash Height=1110 mm  [stored 3.64173 ft]; Sash Width Left=886 mm; Sash Width Right=886 mm; Standard Interlocker=Yes; Width=1790 mm  [stored 5.8727 ft]; Windload Design=1500 mm  [stored 4.92126 ft]
- 540SW-1812XO-2000Pa: Area Left Sash Glazing=0.78 m²; Area Right Sash Glazing=0.78 m²; Clearvue SHGC Value=0.603; Clearvue U Value=6.75; Custom Windload=2000 mm  [stored 6.56168 ft]; Custom Window Height=1190 mm  [stored 3.9042 ft]; Custom Window Width=1790 mm  [stored 5.8727 ft]; Energy Advantage SHGC Value=0.54; Energy Advantage U Value=5.23; Heavy Duty Interlocker=Yes; Height=1190 mm  [stored 3.9042 ft]; Intruderprufe LowE SHGC Value=0.504; Intruderprufe LowE U Value=5.14; Intruderprufe SHGC Value=0.568; Intruderprufe U Value=6.61; Is Heavy Duty Interlocker=1 mm  [stored 0.00328084 ft]; Limit Sash Width Left Max=1200 mm; Limit Sash Width Left Min=572 mm; Max Pane Area=0.78 m²; Sash Height=1110 mm  [stored 3.64173 ft]; Sash Width Left=886 mm; Sash Width Right=886 mm; Standard Interlocker=No; Width=1790 mm  [stored 5.8727 ft]; Windload Design=2000 mm  [stored 6.56168 ft]
- 540SW-1815XO-1500Pa: Area Left Sash Glazing=1.01 m²; Area Right Sash Glazing=1.01 m²; Clearvue SHGC Value=0.627; Clearvue U Value=6.71; Custom Windload=1500 mm  [stored 4.92126 ft]; Custom Window Height=1490 mm  [stored 4.88845 ft]; Custom Window Width=1790 mm  [stored 5.8727 ft]; Energy Advantage SHGC Value=0.562; Energy Advantage U Value=5.11; Heavy Duty Interlocker=Yes; Height=1490 mm  [stored 4.88845 ft]; Intruderprufe LowE SHGC Value=0.524; Intruderprufe LowE U Value=5.02; Intruderprufe SHGC Value=0.591; Intruderprufe U Value=6.56; Is Heavy Duty Interlocker=1 mm  [stored 0.00328084 ft]; Limit Sash Width Left Max=1200 mm; Limit Sash Width Left Min=572 mm; Max Pane Area=1.01 m²; Sash Height=1410 mm; Sash Width Left=886 mm; Sash Width Right=886 mm; Standard Interlocker=No; Width=1790 mm  [stored 5.8727 ft]; Windload Design=1500 mm  [stored 4.92126 ft]
- 540SW-1815XO-2000Pa: Area Left Sash Glazing=1.01 m²; Area Right Sash Glazing=1.01 m²; Clearvue SHGC Value=0.627; Clearvue U Value=6.71; Custom Windload=2000 mm  [stored 6.56168 ft]; Custom Window Height=1490 mm  [stored 4.88845 ft]; Custom Window Width=1790 mm  [stored 5.8727 ft]; Energy Advantage SHGC Value=0.562; Energy Advantage U Value=5.11; Heavy Duty Interlocker=Yes; Height=1490 mm  [stored 4.88845 ft]; Intruderprufe LowE SHGC Value=0.524; Intruderprufe LowE U Value=5.02; Intruderprufe SHGC Value=0.591; Intruderprufe U Value=6.56; Is Heavy Duty Interlocker=1 mm  [stored 0.00328084 ft]; Limit Sash Width Left Max=1200 mm; Limit Sash Width Left Min=572 mm; Max Pane Area=1.01 m²; Sash Height=1410 mm; Sash Width Left=886 mm; Sash Width Right=886 mm; Standard Interlocker=No; Width=1790 mm  [stored 5.8727 ft]; Windload Design=2000 mm  [stored 6.56168 ft]
- 540SW-2106XO-1500Pa: Area Left Sash Glazing=0.37 m²; Area Right Sash Glazing=0.37 m²; Clearvue SHGC Value=0.492; Clearvue U Value=6.92; Custom Windload=1500 mm  [stored 4.92126 ft]; Custom Window Height=590 mm  [stored 1.9357 ft]; Custom Window Width=2090 mm  [stored 6.85696 ft]; Energy Advantage SHGC Value=0.443; Energy Advantage U Value=5.72; Heavy Duty Interlocker=No; Height=590 mm  [stored 1.9357 ft]; Intruderprufe LowE SHGC Value=0.414; Intruderprufe LowE U Value=5.62; Intruderprufe SHGC Value=0.465; Intruderprufe U Value=6.79; Is Heavy Duty Interlocker=0 mm  [stored 0 ft]; Limit Sash Width Left Max=1200 mm; Limit Sash Width Left Min=872 mm; Max Pane Area=0.37 m²; Sash Height=510 mm; Sash Width Left=1036 mm; Sash Width Right=1036 mm; Standard Interlocker=Yes; Width=2090 mm  [stored 6.85696 ft]; Windload Design=1500 mm  [stored 4.92126 ft]
- 540SW-2106XO-2000Pa: Area Left Sash Glazing=0.37 m²; Area Right Sash Glazing=0.37 m²; Clearvue SHGC Value=0.492; Clearvue U Value=6.92; Custom Windload=2000 mm  [stored 6.56168 ft]; Custom Window Height=590 mm  [stored 1.9357 ft]; Custom Window Width=2090 mm  [stored 6.85696 ft]; Energy Advantage SHGC Value=0.443; Energy Advantage U Value=5.72; Heavy Duty Interlocker=No; Height=590 mm  [stored 1.9357 ft]; Intruderprufe LowE SHGC Value=0.414; Intruderprufe LowE U Value=5.62; Intruderprufe SHGC Value=0.465; Intruderprufe U Value=6.79; Is Heavy Duty Interlocker=0 mm  [stored 0 ft]; Limit Sash Width Left Max=1200 mm; Limit Sash Width Left Min=872 mm; Max Pane Area=0.37 m²; Sash Height=510 mm; Sash Width Left=1036 mm; Sash Width Right=1036 mm; Standard Interlocker=Yes; Width=2090 mm  [stored 6.85696 ft]; Windload Design=2000 mm  [stored 6.56168 ft]
- 540SW-2109XO-1500Pa: Area Left Sash Glazing=0.65 m²; Area Right Sash Glazing=0.65 m²; Clearvue SHGC Value=0.576; Clearvue U Value=6.76; Custom Windload=1500 mm  [stored 4.92126 ft]; Custom Window Height=890 mm  [stored 2.91995 ft]; Custom Window Width=2090 mm  [stored 6.85696 ft]; Energy Advantage SHGC Value=0.517; Energy Advantage U Value=5.32; Heavy Duty Interlocker=No; Height=890 mm  [stored 2.91995 ft]; Intruderprufe LowE SHGC Value=0.483; Intruderprufe LowE U Value=5.22; Intruderprufe SHGC Value=0.543; Intruderprufe U Value=6.62; Is Heavy Duty Interlocker=0 mm  [stored 0 ft]; Limit Sash Width Left Max=1200 mm; Limit Sash Width Left Min=872 mm; Max Pane Area=0.65 m²; Sash Height=810 mm  [stored 2.65748 ft]; Sash Width Left=1036 mm; Sash Width Right=1036 mm; Standard Interlocker=Yes; Width=2090 mm  [stored 6.85696 ft]; Windload Design=1500 mm  [stored 4.92126 ft]
- 540SW-2109XO-2000Pa: Area Left Sash Glazing=0.65 m²; Area Right Sash Glazing=0.65 m²; Clearvue SHGC Value=0.576; Clearvue U Value=6.76; Custom Windload=2000 mm  [stored 6.56168 ft]; Custom Window Height=890 mm  [stored 2.91995 ft]; Custom Window Width=2090 mm  [stored 6.85696 ft]; Energy Advantage SHGC Value=0.517; Energy Advantage U Value=5.32; Heavy Duty Interlocker=No; Height=890 mm  [stored 2.91995 ft]; Intruderprufe LowE SHGC Value=0.483; Intruderprufe LowE U Value=5.22; Intruderprufe SHGC Value=0.543; Intruderprufe U Value=6.62; Is Heavy Duty Interlocker=0 mm  [stored 0 ft]; Limit Sash Width Left Max=1200 mm; Limit Sash Width Left Min=872 mm; Max Pane Area=0.65 m²; Sash Height=810 mm  [stored 2.65748 ft]; Sash Width Left=1036 mm; Sash Width Right=1036 mm; Standard Interlocker=Yes; Width=2090 mm  [stored 6.85696 ft]; Windload Design=2000 mm  [stored 6.56168 ft]
- 540SW-2112XO-1500Pa: Area Left Sash Glazing=0.93 m²; Area Right Sash Glazing=0.93 m²; Clearvue SHGC Value=0.617; Clearvue U Value=6.68; Custom Windload=1500 mm  [stored 4.92126 ft]; Custom Window Height=1190 mm  [stored 3.9042 ft]; Custom Window Width=2090 mm  [stored 6.85696 ft]; Energy Advantage SHGC Value=0.554; Energy Advantage U Value=5.12; Heavy Duty Interlocker=No; Height=1190 mm  [stored 3.9042 ft]; Intruderprufe LowE SHGC Value=0.516; Intruderprufe LowE U Value=5.03; Intruderprufe SHGC Value=0.582; Intruderprufe U Value=6.53; Is Heavy Duty Interlocker=0 mm  [stored 0 ft]; Limit Sash Width Left Max=1200 mm; Limit Sash Width Left Min=872 mm; Max Pane Area=0.93 m²; Sash Height=1110 mm  [stored 3.64173 ft]; Sash Width Left=1036 mm; Sash Width Right=1036 mm; Standard Interlocker=Yes; Width=2090 mm  [stored 6.85696 ft]; Windload Design=1500 mm  [stored 4.92126 ft]
- 540SW-2112XO-2000Pa: Area Left Sash Glazing=0.93 m²; Area Right Sash Glazing=0.93 m²; Clearvue SHGC Value=0.617; Clearvue U Value=6.68; Custom Windload=2000 mm  [stored 6.56168 ft]; Custom Window Height=1190 mm  [stored 3.9042 ft]; Custom Window Width=2090 mm  [stored 6.85696 ft]; Energy Advantage SHGC Value=0.554; Energy Advantage U Value=5.12; Heavy Duty Interlocker=Yes; Height=1190 mm  [stored 3.9042 ft]; Intruderprufe LowE SHGC Value=0.516; Intruderprufe LowE U Value=5.03; Intruderprufe SHGC Value=0.582; Intruderprufe U Value=6.53; Is Heavy Duty Interlocker=1 mm  [stored 0.00328084 ft]; Limit Sash Width Left Max=1200 mm; Limit Sash Width Left Min=872 mm; Max Pane Area=0.93 m²; Sash Height=1110 mm  [stored 3.64173 ft]; Sash Width Left=1036 mm; Sash Width Right=1036 mm; Standard Interlocker=No; Width=2090 mm  [stored 6.85696 ft]; Windload Design=2000 mm  [stored 6.56168 ft]
- 540SW-2115XO-1500Pa: Area Left Sash Glazing=1.21 m²; Area Right Sash Glazing=1.21 m²; Clearvue SHGC Value=0.642; Clearvue U Value=6.63; Custom Windload=1500 mm  [stored 4.92126 ft]; Custom Window Height=1490 mm  [stored 4.88845 ft]; Custom Window Width=2090 mm  [stored 6.85696 ft]; Energy Advantage SHGC Value=0.576; Energy Advantage U Value=5; Heavy Duty Interlocker=Yes; Height=1490 mm  [stored 4.88845 ft]; Intruderprufe LowE SHGC Value=0.536; Intruderprufe LowE U Value=4.91; Intruderprufe SHGC Value=0.606; Intruderprufe U Value=6.48; Is Heavy Duty Interlocker=1 mm  [stored 0.00328084 ft]; Limit Sash Width Left Max=1200 mm; Limit Sash Width Left Min=872 mm; Max Pane Area=1.21 m²; Sash Height=1410 mm; Sash Width Left=1036 mm; Sash Width Right=1036 mm; Standard Interlocker=No; Width=2090 mm  [stored 6.85696 ft]; Windload Design=1500 mm  [stored 4.92126 ft]
- 540SW-2115XO-2000Pa: Area Left Sash Glazing=1.21 m²; Area Right Sash Glazing=1.21 m²; Clearvue SHGC Value=0.642; Clearvue U Value=6.63; Custom Windload=2000 mm  [stored 6.56168 ft]; Custom Window Height=1490 mm  [stored 4.88845 ft]; Custom Window Width=2090 mm  [stored 6.85696 ft]; Energy Advantage SHGC Value=0.576; Energy Advantage U Value=5; Heavy Duty Interlocker=Yes; Height=1490 mm  [stored 4.88845 ft]; Intruderprufe LowE SHGC Value=0.536; Intruderprufe LowE U Value=4.91; Intruderprufe SHGC Value=0.606; Intruderprufe U Value=6.48; Is Heavy Duty Interlocker=1 mm  [stored 0.00328084 ft]; Limit Sash Width Left Max=1200 mm; Limit Sash Width Left Min=872 mm; Max Pane Area=1.21 m²; Sash Height=1410 mm; Sash Width Left=1036 mm; Sash Width Right=1036 mm; Standard Interlocker=No; Width=2090 mm  [stored 6.85696 ft]; Windload Design=2000 mm  [stored 6.56168 ft]
- 540SW-2406XO-1500Pa: Area Left Sash Glazing=0.43 m²; Area Right Sash Glazing=0.43 m²; Clearvue SHGC Value=0.501; Clearvue U Value=6.88; Custom Windload=1500 mm  [stored 4.92126 ft]; Custom Window Height=590 mm  [stored 1.9357 ft]; Custom Window Width=2390 mm  [stored 7.84121 ft]; Energy Advantage SHGC Value=0.45; Energy Advantage U Value=5.65; Heavy Duty Interlocker=No; Height=590 mm  [stored 1.9357 ft]; Intruderprufe LowE SHGC Value=0.421; Intruderprufe LowE U Value=5.56; Intruderprufe SHGC Value=0.473; Intruderprufe U Value=6.75; Is Heavy Duty Interlocker=0 mm  [stored 0 ft]; Limit Sash Width Left Max=1200 mm; Limit Sash Width Left Min=1172 mm; Max Pane Area=0.43 m²; Sash Height=510 mm; Sash Width Left=1186 mm; Sash Width Right=1186 mm; Standard Interlocker=Yes; Width=2390 mm  [stored 7.84121 ft]; Windload Design=1500 mm  [stored 4.92126 ft]
- 540SW-2406XO-2000Pa: Area Left Sash Glazing=0.43 m²; Area Right Sash Glazing=0.43 m²; Clearvue SHGC Value=0.501; Clearvue U Value=6.88; Custom Windload=2000 mm  [stored 6.56168 ft]; Custom Window Height=590 mm  [stored 1.9357 ft]; Custom Window Width=2390 mm  [stored 7.84121 ft]; Energy Advantage SHGC Value=0.45; Energy Advantage U Value=5.65; Heavy Duty Interlocker=No; Height=590 mm  [stored 1.9357 ft]; Intruderprufe LowE SHGC Value=0.421; Intruderprufe LowE U Value=5.56; Intruderprufe SHGC Value=0.473; Intruderprufe U Value=6.75; Is Heavy Duty Interlocker=0 mm  [stored 0 ft]; Limit Sash Width Left Max=1200 mm; Limit Sash Width Left Min=1172 mm; Max Pane Area=0.43 m²; Sash Height=510 mm; Sash Width Left=1186 mm; Sash Width Right=1186 mm; Standard Interlocker=Yes; Width=2390 mm  [stored 7.84121 ft]; Windload Design=2000 mm  [stored 6.56168 ft]
- 540SW-2409XO-1500Pa: Area Left Sash Glazing=0.76 m²; Area Right Sash Glazing=0.76 m²; Clearvue SHGC Value=0.586; Clearvue U Value=6.7; Custom Windload=1500 mm  [stored 4.92126 ft]; Custom Window Height=890 mm  [stored 2.91995 ft]; Custom Window Width=2390 mm  [stored 7.84121 ft]; Energy Advantage SHGC Value=0.526; Energy Advantage U Value=5.24; Heavy Duty Interlocker=No; Height=890 mm  [stored 2.91995 ft]; Intruderprufe LowE SHGC Value=0.491; Intruderprufe LowE U Value=5.15; Intruderprufe SHGC Value=0.553; Intruderprufe U Value=6.57; Is Heavy Duty Interlocker=0 mm  [stored 0 ft]; Limit Sash Width Left Max=1200 mm; Limit Sash Width Left Min=1172 mm; Max Pane Area=0.76 m²; Sash Height=810 mm  [stored 2.65748 ft]; Sash Width Left=1186 mm; Sash Width Right=1186 mm; Standard Interlocker=Yes; Width=2390 mm  [stored 7.84121 ft]; Windload Design=1500 mm  [stored 4.92126 ft]
- 540SW-2409XO-2000Pa: Area Left Sash Glazing=0.76 m²; Area Right Sash Glazing=0.76 m²; Clearvue SHGC Value=0.586; Clearvue U Value=6.7; Custom Windload=2000 mm  [stored 6.56168 ft]; Custom Window Height=890 mm  [stored 2.91995 ft]; Custom Window Width=2390 mm  [stored 7.84121 ft]; Energy Advantage SHGC Value=0.526; Energy Advantage U Value=5.24; Heavy Duty Interlocker=No; Height=890 mm  [stored 2.91995 ft]; Intruderprufe LowE SHGC Value=0.491; Intruderprufe LowE U Value=5.15; Intruderprufe SHGC Value=0.553; Intruderprufe U Value=6.57; Is Heavy Duty Interlocker=0 mm  [stored 0 ft]; Limit Sash Width Left Max=1200 mm; Limit Sash Width Left Min=1172 mm; Max Pane Area=0.76 m²; Sash Height=810 mm  [stored 2.65748 ft]; Sash Width Left=1186 mm; Sash Width Right=1186 mm; Standard Interlocker=Yes; Width=2390 mm  [stored 7.84121 ft]; Windload Design=2000 mm  [stored 6.56168 ft]
- 540SW-2412XO-1500Pa: Area Left Sash Glazing=1.08 m²; Area Right Sash Glazing=1.08 m²; Clearvue SHGC Value=0.629; Clearvue U Value=6.62; Custom Windload=1500 mm  [stored 4.92126 ft]; Custom Window Height=1190 mm  [stored 3.9042 ft]; Custom Window Width=2390 mm  [stored 7.84121 ft]; Energy Advantage SHGC Value=0.564; Energy Advantage U Value=5.03; Heavy Duty Interlocker=No; Height=1190 mm  [stored 3.9042 ft]; Intruderprufe LowE SHGC Value=0.525; Intruderprufe LowE U Value=4.94; Intruderprufe SHGC Value=0.593; Intruderprufe U Value=6.48; Is Heavy Duty Interlocker=0 mm  [stored 0 ft]; Limit Sash Width Left Max=1200 mm; Limit Sash Width Left Min=1172 mm; Max Pane Area=1.08 m²; Sash Height=1110 mm  [stored 3.64173 ft]; Sash Width Left=1186 mm; Sash Width Right=1186 mm; Standard Interlocker=Yes; Width=2390 mm  [stored 7.84121 ft]; Windload Design=1500 mm  [stored 4.92126 ft]
- 540SW-2412XO-2000Pa: Area Left Sash Glazing=1.08 m²; Area Right Sash Glazing=1.08 m²; Clearvue SHGC Value=0.629; Clearvue U Value=6.62; Custom Windload=2000 mm  [stored 6.56168 ft]; Custom Window Height=1190 mm  [stored 3.9042 ft]; Custom Window Width=2390 mm  [stored 7.84121 ft]; Energy Advantage SHGC Value=0.564; Energy Advantage U Value=5.03; Heavy Duty Interlocker=Yes; Height=1190 mm  [stored 3.9042 ft]; Intruderprufe LowE SHGC Value=0.525; Intruderprufe LowE U Value=4.94; Intruderprufe SHGC Value=0.593; Intruderprufe U Value=6.48; Is Heavy Duty Interlocker=1 mm  [stored 0.00328084 ft]; Limit Sash Width Left Max=1200 mm; Limit Sash Width Left Min=1172 mm; Max Pane Area=1.08 m²; Sash Height=1110 mm  [stored 3.64173 ft]; Sash Width Left=1186 mm; Sash Width Right=1186 mm; Standard Interlocker=No; Width=2390 mm  [stored 7.84121 ft]; Windload Design=2000 mm  [stored 6.56168 ft]
- 540SW-2415XO-1500Pa: Area Left Sash Glazing=1.4 m²; Area Right Sash Glazing=1.4 m²; Clearvue SHGC Value=0.654; Clearvue U Value=6.57; Custom Windload=1500 mm  [stored 4.92126 ft]; Custom Window Height=1490 mm  [stored 4.88845 ft]; Custom Window Width=2390 mm  [stored 7.84121 ft]; Energy Advantage SHGC Value=0.586; Energy Advantage U Value=4.91; Heavy Duty Interlocker=Yes; Height=1490 mm  [stored 4.88845 ft]; Intruderprufe LowE SHGC Value=0.546; Intruderprufe LowE U Value=4.82; Intruderprufe SHGC Value=0.617; Intruderprufe U Value=6.43; Is Heavy Duty Interlocker=1 mm  [stored 0.00328084 ft]; Limit Sash Width Left Max=1200 mm; Limit Sash Width Left Min=1172 mm; Max Pane Area=1.4 m²; Sash Height=1410 mm; Sash Width Left=1186 mm; Sash Width Right=1186 mm; Standard Interlocker=No; Width=2390 mm  [stored 7.84121 ft]; Windload Design=1500 mm  [stored 4.92126 ft]
- 540SW-2415XO-2000Pa: Area Left Sash Glazing=1.4 m²; Area Right Sash Glazing=1.4 m²; Clearvue SHGC Value=0.654; Clearvue U Value=6.57; Custom Windload=2000 mm  [stored 6.56168 ft]; Custom Window Height=1490 mm  [stored 4.88845 ft]; Custom Window Width=2390 mm  [stored 7.84121 ft]; Energy Advantage SHGC Value=0.586; Energy Advantage U Value=4.91; Heavy Duty Interlocker=Yes; Height=1490 mm  [stored 4.88845 ft]; Intruderprufe LowE SHGC Value=0.546; Intruderprufe LowE U Value=4.82; Intruderprufe SHGC Value=0.617; Intruderprufe U Value=6.43; Is Heavy Duty Interlocker=1 mm  [stored 0.00328084 ft]; Limit Sash Width Left Max=1200 mm; Limit Sash Width Left Min=1172 mm; Max Pane Area=1.4 m²; Sash Height=1410 mm; Sash Width Left=1186 mm; Sash Width Right=1186 mm; Standard Interlocker=No; Width=2390 mm  [stored 7.84121 ft]; Windload Design=2000 mm  [stored 6.56168 ft]

note: [stored X ft] marks values corroborated as IEEE doubles in the binary element streams (Revit-internal decimal feet)

## geometry (parser evidence)
native form markers: Sweep x9
no freeform markers — native parametric forms only
